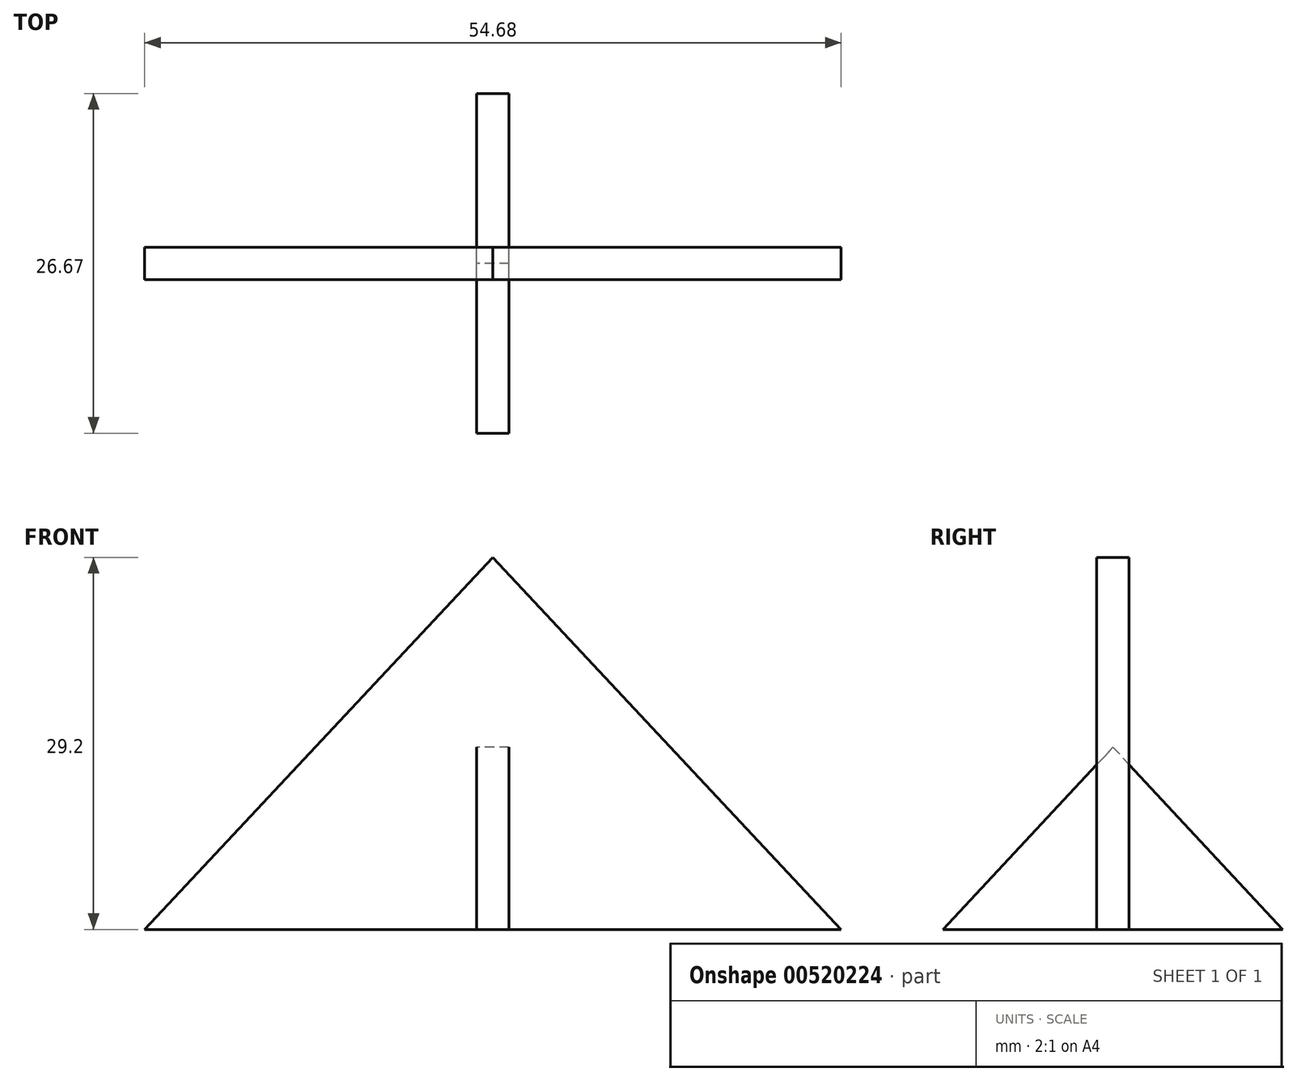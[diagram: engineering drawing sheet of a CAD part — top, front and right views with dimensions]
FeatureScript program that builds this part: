
annotation { "Feature Type Name" : "Feature", "Feature Type Description" : "" }
export const myFeature = defineFeature(function(context is Context, id is Id, definition is map)
    precondition{}
    {
        {
            var Q0;
            Q0=qCreatedBy(makeId("Front.planeOp"),FACE);
            var sketch = newSketch(context, id + "F0", { "sketchPlane" : qUnion([Q0])});
            skLineSegment(sketch, "E0", {"start": v(-27.34, 0) * mm, "end": v(27.34, 0) * mm});
            skLineSegment(sketch, "E1", {"start": v(27.34, 0) * mm, "end": v(0, 29.2) * mm});
            skLineSegment(sketch, "E2", {"start": v(0, 29.2) * mm, "end": v(-27.34, 0) * mm});
            skSolve(sketch);
        }
        {
            var Q0;
            Q0=makeQuery(id+"F0.imprint","IMPRINT",FACE,{"disambiguationData":[TD([[makeQuery(id+"F0.imprint","IMPRINT",EDGE,{"derivedFrom":sQuery(id+"F0.wireOp",EDGE,"E0")}),1.0]])]});
            extrude(context, id + "F1", {"entities" : qUnion([Q0]), "endBound" : BoundingType.SYMMETRIC, "depth" : 2.54 * mm, "offsetDistance" : 25.4 * mm});
        }
        {
            var Q0;
            Q0=qCreatedBy(makeId("Right.planeOp"),FACE);
            var sketch = newSketch(context, id + "F2", { "sketchPlane" : qUnion([Q0])});
            skLineSegment(sketch, "E3", {"start": v(-13.34, 0) * mm, "end": v(13.33, 0) * mm});
            skLineSegment(sketch, "E4", {"start": v(-13.34, 0) * mm, "end": v(0, 14.3) * mm});
            skLineSegment(sketch, "E5", {"start": v(0, 14.3) * mm, "end": v(13.33, 0) * mm});
            skSolve(sketch);
        }
        {
            var Q0;
            Q0 = qSketchRegion(id + "F2", true);
            extrude(context, id + "F3", {"entities" : qUnion([Q0]), "endBound" : BoundingType.SYMMETRIC, "depth" : 2.54 * mm, "offsetDistance" : 25.4 * mm});
        }
    });
